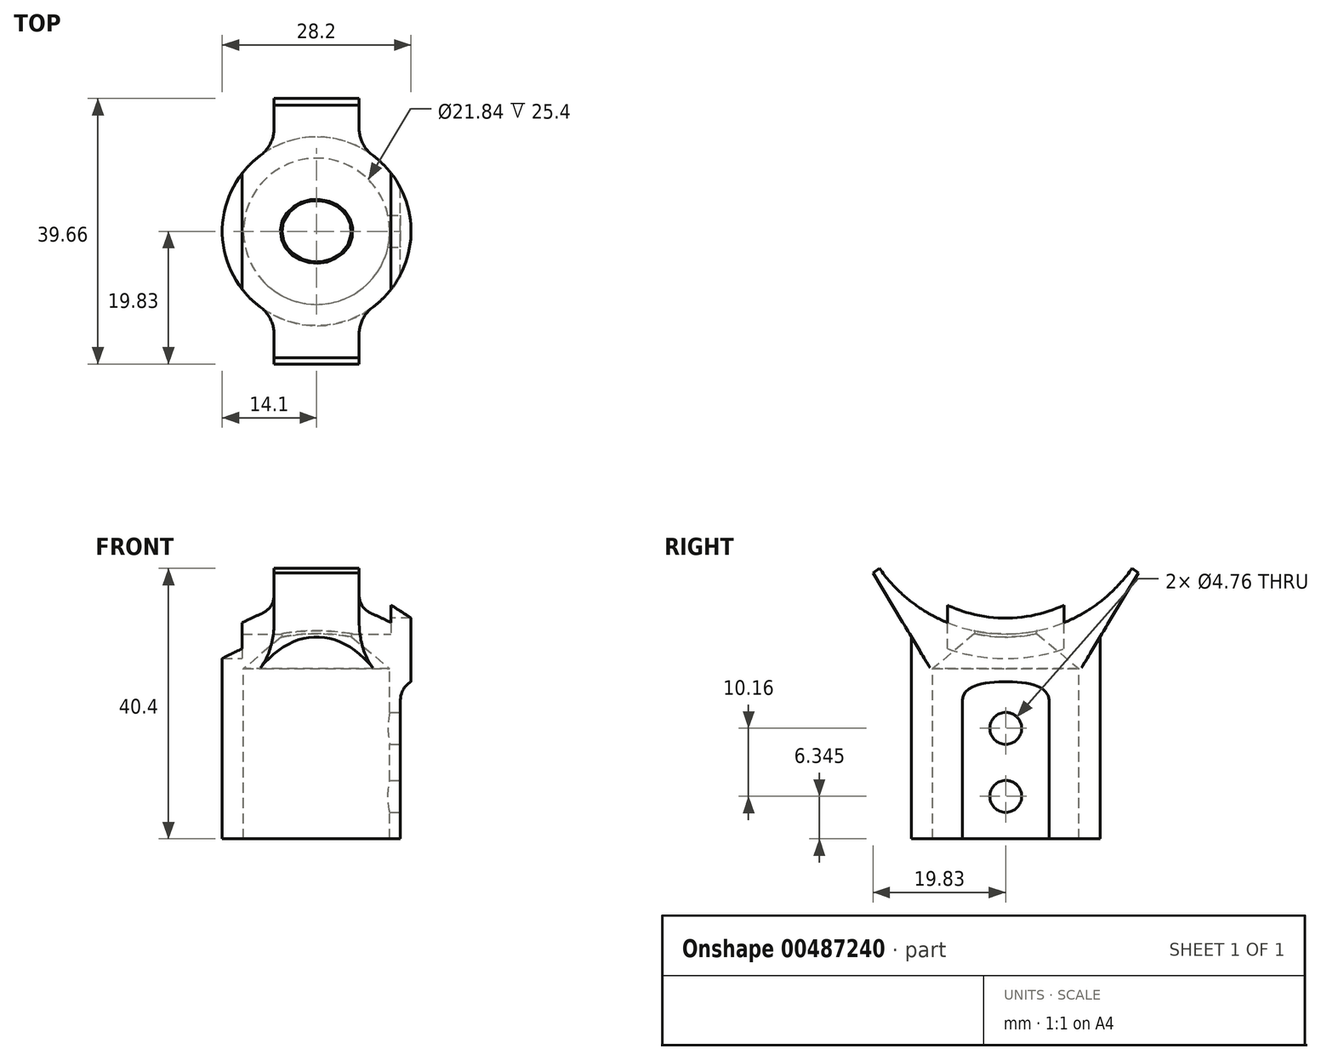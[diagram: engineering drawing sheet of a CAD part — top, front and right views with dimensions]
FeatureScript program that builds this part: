
annotation { "Feature Type Name" : "Feature", "Feature Type Description" : "" }
export const myFeature = defineFeature(function(context is Context, id is Id, definition is map)
    precondition{}
    {
        {
            var Q0;
            Q0=qCreatedBy(makeId("Front.planeOp"),FACE);
            var sketch = newSketch(context, id + "F0", { "sketchPlane" : qUnion([Q0])});
            skLineSegment(sketch, "E0", {"start": v(0, 0) * mm, "end": v(-10.92, -9.16) * mm});
            skLineSegment(sketch, "E1", {"start": v(-10.92, -9.16) * mm, "end": v(-10.92, -34.56) * mm});
            skLineSegment(sketch, "E2", {"start": v(0, 0) * mm, "end": v(0, -71.28) * mm, "construction": true});
            skLineSegment(sketch, "E3", {"start": v(-10.92, -34.56) * mm, "end": v(-14.1, -34.56) * mm});
            skLineSegment(sketch, "E4", {"start": v(-14.1, -34.56) * mm, "end": v(-14.1, 9.52) * mm});
            skLineSegment(sketch, "E5", {"start": v(-14.1, 9.52) * mm, "end": v(0, 9.52) * mm});
            skLineSegment(sketch, "E6", {"start": v(0, 9.52) * mm, "end": v(0, 0) * mm});
            skSolve(sketch);
        }
        {
            var Q0;
            Q0=makeQuery(id+"F0.imprint","IMPRINT",FACE,{"disambiguationData":[TD([[makeQuery(id+"F0.imprint","IMPRINT",EDGE,{"derivedFrom":sQuery(id+"F0.wireOp",EDGE,"E0")}),-1.0]])]});
            var Q1;
            Q1=sQuery(id+"F0.wireOp",EDGE,"E2");
            revolve(context, id + "F1", {"entities" : qUnion([Q0]), "axis" : qUnion([Q1]), "revolveType" : RevolveType.FULL});
        }
        {
            var Q0;
            Q0=makeQuery(id+"F1.opRevolve","SWEPT_EDGE",EDGE,{"disambiguationData":[OSD([sQuery(id+"F0.wireOp",EDGE,"E4"),sQuery(id+"F0.wireOp",EDGE,"E5")])]});
            fillet(context, id + "F2", {"entities" : qUnion([Q0]), "radius" : 2.38 * mm, "tangentPropagation" : true, "allowEdgeOverflow" : false});
        }
        {
            var Q0;
            Q0=qCreatedBy(makeId("Front.planeOp"),FACE);
            var sketch = newSketch(context, id + "F3", { "sketchPlane" : qUnion([Q0])});
            skLineSegment(sketch, "E7", {"start": v(10.92, -10.67) * mm, "end": v(10.92, -36.07) * mm});
            skLineSegment(sketch, "E8", {"start": v(-10.92, -36.07) * mm, "end": v(-10.92, -10.67) * mm});
            skLineSegment(sketch, "E9", {"start": v(-14.1, -36.07) * mm, "end": v(-14.1, 3.17) * mm});
            skLineSegment(sketch, "E10", {"start": v(12.5, -13.84) * mm, "end": v(12.5, -38.6) * mm});
            skLineSegment(sketch, "E11", {"start": v(15.68, -10.67) * mm, "end": v(18.86, -10.67) * mm});
            skLineSegment(sketch, "E12", {"start": v(18.86, -10.67) * mm, "end": v(18.86, -38.6) * mm});
            skLineSegment(sketch, "E13", {"start": v(18.86, -38.6) * mm, "end": v(12.5, -38.6) * mm});
            skPoint(sketch, "E14.visualSharp", {"position": v(12.5, -10.67) * mm});
            skArc(sketch, "E14.filletArc", {"start": v(15.68, -10.67) * mm, "mid": v(13.44, -11.6) * mm, "end": v(12.5, -13.84) * mm});
            skSolve(sketch);
        }
        {
            var Q0;
            Q0=makeQuery(id+"F3.imprint","IMPRINT",FACE,{"disambiguationData":[TD([[makeQuery(id+"F3.imprint","IMPRINT",EDGE,{"derivedFrom":sQuery(id+"F3.wireOp",EDGE,"E10")}),1.0]])]});
            extrude(context, id + "F4", {"entities" : qUnion([Q0]), "operationType" : NewBodyOperationType.REMOVE, "depth" : 25.4 * mm, "hasSecondDirection" : true, "secondDirectionOppositeDirection" : true, "secondDirectionDepth" : 25.4 * mm});
        }
        {
            var Q0;
            Q0=makeQuery(id+"F4.boolean.opBoolean","COPY",FACE,{"derivedFrom":makeQuery(id+"F4.opExtrude","SWEPT_FACE",FACE,{"disambiguationData":[OSD([sQuery(id+"F3.wireOp",EDGE,"E10")])]})});
            var sketch = newSketch(context, id + "F5", { "sketchPlane" : qUnion([Q0])});
            skLineSegment(sketch, "E15", {"start": v(0, -34.56) * mm, "end": v(0, -13.84) * mm, "construction": true});
            skCircle(sketch, "E16", {"center": v(0, -18.05) * mm, "radius": 2.38 * mm});
            skCircle(sketch, "E17", {"center": v(0, -28.21) * mm, "radius": 2.38 * mm});
            skSolve(sketch);
        }
        {
            var Q0;
            Q0=makeQuery(id+"F5.imprint","IMPRINT",FACE,{"disambiguationData":[TD([[makeQuery(id+"F5.imprint","IMPRINT",EDGE,{"derivedFrom":sQuery(id+"F5.wireOp",EDGE,"E16")}),1.0]])]});
            var Q1;
            Q1=makeQuery(id+"F5.imprint","IMPRINT",FACE,{"disambiguationData":[TD([[makeQuery(id+"F5.imprint","IMPRINT",EDGE,{"derivedFrom":sQuery(id+"F5.wireOp",EDGE,"E17")}),1.0]])]});
            extrude(context, id + "F6", {"entities" : qUnion([Q0, Q1]), "operationType" : NewBodyOperationType.REMOVE, "oppositeDirection" : true, "depth" : 6.35 * mm});
        }
        {
            var Q0;
            Q0=qCreatedBy(makeId("Right.planeOp"),FACE);
            var sketch = newSketch(context, id + "F7", { "sketchPlane" : qUnion([Q0])});
            skLineSegment(sketch, "E18", {"start": v(-11.12, -9.33) * mm, "end": v(0, 0) * mm});
            skLineSegment(sketch, "E19", {"start": v(0, 0) * mm, "end": v(11.12, -9.33) * mm});
            skLineSegment(sketch, "E20", {"start": v(-11.12, -9.33) * mm, "end": v(-21.59, 8.08) * mm});
            skLineSegment(sketch, "E21", {"start": v(0, 0) * mm, "end": v(0, 19.05) * mm, "construction": true});
            skLineSegment(sketch, "E22.MirrorCS", {"start": v(11.12, -9.33) * mm, "end": v(21.59, 8.08) * mm});
            skLineSegment(sketch, "E23", {"start": v(-21.6, 8.08) * mm, "end": v(21.59, 8.08) * mm});
            skCircle(sketch, "E24", {"center": v(0, 19.05) * mm, "radius": 23.03 * mm, "construction": true});
            skLineSegment(sketch, "E25", {"start": v(-15.66, 8.08) * mm, "end": v(-19.83, 5.16) * mm});
            skLineSegment(sketch, "E26.MirrorCS", {"start": v(15.66, 8.08) * mm, "end": v(19.83, 5.16) * mm});
            skPoint(sketch, "E27.orphan", {"position": v(-25.04, 1.52) * mm});
            skPoint(sketch, "E28.orphan", {"position": v(25.04, 1.52) * mm});
            skSolve(sketch);
        }
        {
            var Q0;
            Q0=makeQuery(id+"F7.imprint","IMPRINT",FACE,{"disambiguationData":[TD([[makeQuery(id+"F7.imprint","IMPRINT",EDGE,{"derivedFrom":sQuery(id+"F7.wireOp",EDGE,"E18")}),1.0]])]});
            extrude(context, id + "F8", {"entities" : qUnion([Q0]), "operationType" : NewBodyOperationType.ADD, "depth" : 6.35 * mm, "offsetDistance" : 25.4 * mm, "hasSecondDirection" : true, "secondDirectionOppositeDirection" : true, "secondDirectionDepth" : 6.35 * mm});
        }
        {
            var Q0;
            Q0=qCreatedBy(makeId("Right.planeOp"),FACE);
            var sketch = newSketch(context, id + "F9", { "sketchPlane" : qUnion([Q0])});
            skCircle(sketch, "E29.0", {"center": v(0, 19.05) * mm, "radius": 23.03 * mm});
            skSolve(sketch);
        }
        {
            var Q0;
            Q0=makeQuery(id+"F9.imprint","IMPRINT",FACE,{"disambiguationData":[TD([[makeQuery(id+"F9.imprint","IMPRINT",EDGE,{"derivedFrom":sQuery(id+"F9.wireOp",EDGE,"E29.0")}),1.0]])]});
            extrude(context, id + "F10", {"entities" : qUnion([Q0]), "operationType" : NewBodyOperationType.REMOVE, "oppositeDirection" : true, "depth" : 25.4 * mm, "offsetDistance" : 25.4 * mm, "hasSecondDirection" : true, "secondDirectionOppositeDirection" : false, "secondDirectionDepth" : 11.1 * mm});
        }
        {
            var Q0;
            Q0=makeQuery(id+"F8.boolean.opBoolean","INTERSECT",EDGE,{"disambiguationData":[OD(0.0)],"derivedFrom":[makeQuery(id+"F1.opRevolve","SWEPT_FACE",FACE,{"disambiguationData":[OSD([sQuery(id+"F0.wireOp",EDGE,"E4")])]}),makeQuery(id+"F8.opExtrude","CAP_FACE",FACE,{"disambiguationData":[OSD([sQuery(id+"F7.wireOp",EDGE,"E18"),sQuery(id+"F7.wireOp",EDGE,"E19"),sQuery(id+"F7.wireOp",EDGE,"E20"),sQuery(id+"F7.wireOp",EDGE,"E22.MirrorCS"),sQuery(id+"F7.wireOp",EDGE,"E23")])],"isStart":false})]});
            var Q1;
            Q1=makeQuery(id+"F8.boolean.opBoolean","INTERSECT",EDGE,{"disambiguationData":[OD(1.0)],"derivedFrom":[makeQuery(id+"F1.opRevolve","SWEPT_FACE",FACE,{"disambiguationData":[OSD([sQuery(id+"F0.wireOp",EDGE,"E4")])]}),makeQuery(id+"F8.opExtrude","CAP_FACE",FACE,{"disambiguationData":[OSD([sQuery(id+"F7.wireOp",EDGE,"E18"),sQuery(id+"F7.wireOp",EDGE,"E19"),sQuery(id+"F7.wireOp",EDGE,"E20"),sQuery(id+"F7.wireOp",EDGE,"E22.MirrorCS"),sQuery(id+"F7.wireOp",EDGE,"E23")])],"isStart":false})]});
            var Q2;
            Q2=makeQuery(id+"F8.boolean.opBoolean","INTERSECT",EDGE,{"disambiguationData":[OD(1.0)],"derivedFrom":[makeQuery(id+"F1.opRevolve","SWEPT_FACE",FACE,{"disambiguationData":[OSD([sQuery(id+"F0.wireOp",EDGE,"E4")])]}),makeQuery(id+"F8.opExtrude","CAP_FACE",FACE,{"disambiguationData":[OSD([sQuery(id+"F7.wireOp",EDGE,"E18"),sQuery(id+"F7.wireOp",EDGE,"E19"),sQuery(id+"F7.wireOp",EDGE,"E20"),sQuery(id+"F7.wireOp",EDGE,"E22.MirrorCS"),sQuery(id+"F7.wireOp",EDGE,"E23")])],"isStart":true})]});
            var Q3;
            Q3=makeQuery(id+"F8.boolean.opBoolean","INTERSECT",EDGE,{"disambiguationData":[OD(0.0)],"derivedFrom":[makeQuery(id+"F1.opRevolve","SWEPT_FACE",FACE,{"disambiguationData":[OSD([sQuery(id+"F0.wireOp",EDGE,"E4")])]}),makeQuery(id+"F8.opExtrude","CAP_FACE",FACE,{"disambiguationData":[OSD([sQuery(id+"F7.wireOp",EDGE,"E18"),sQuery(id+"F7.wireOp",EDGE,"E19"),sQuery(id+"F7.wireOp",EDGE,"E20"),sQuery(id+"F7.wireOp",EDGE,"E22.MirrorCS"),sQuery(id+"F7.wireOp",EDGE,"E23")])],"isStart":true})]});
            fillet(context, id + "F11", {"entities" : qUnion([Q0, Q1, Q2, Q3]), "radius" : 5.08 * mm, "tangentPropagation" : true, "allowEdgeOverflow" : false});
        }
        {
            var Q0;
            Q0=qCreatedBy(makeId("Right.planeOp"),FACE);
            var sketch = newSketch(context, id + "F12", { "sketchPlane" : qUnion([Q0])});
            skCircle(sketch, "E30", {"center": v(0, 19.05) * mm, "radius": 20.64 * mm});
            skSolve(sketch);
        }
        {
            var Q0;
            Q0=makeQuery(id+"F12.imprint","IMPRINT",FACE,{"disambiguationData":[TD([[makeQuery(id+"F12.imprint","IMPRINT",EDGE,{"derivedFrom":sQuery(id+"F12.wireOp",EDGE,"E30")}),1.0]])]});
            extrude(context, id + "F13", {"entities" : qUnion([Q0]), "operationType" : NewBodyOperationType.REMOVE, "depth" : 25.4 * mm, "offsetDistance" : 25.4 * mm});
        }
        {
            var Q0;
            Q0=qCreatedBy(makeId("Right.planeOp"),FACE);
            cPlane(context, id + "F14", {"entities" : qUnion([Q0]), "cplaneType" : CPlaneType.OFFSET, "offset" : 11.1 * mm, "oppositeDirection" : true, "width" : 152.4 * mm, "height" : 152.4 * mm});
        }
        {
            var Q0;
            Q0=qCreatedBy(id+"F14.planeOp",FACE);
            var sketch = newSketch(context, id + "F15", { "sketchPlane" : qUnion([Q0])});
            skPoint(sketch, "E31.0", {"position": v(0, 19.05) * mm});
            skCircle(sketch, "E32", {"center": v(0, 19.05) * mm, "radius": 26.67 * mm});
            skSolve(sketch);
        }
        {
            var Q0;
            Q0=makeQuery(id+"F15.imprint","IMPRINT",FACE,{"disambiguationData":[TD([[makeQuery(id+"F15.imprint","IMPRINT",EDGE,{"derivedFrom":sQuery(id+"F15.wireOp",EDGE,"E32")}),1.0]])]});
            extrude(context, id + "F16", {"entities" : qUnion([Q0]), "operationType" : NewBodyOperationType.REMOVE, "oppositeDirection" : true, "depth" : 25.4 * mm, "offsetDistance" : 25.4 * mm});
        }
        {
            var Q0;
            Q0=makeQuery(id+"F10.boolean.opBoolean","INTERSECT",EDGE,{"derivedFrom":[makeQuery(id+"F1.opRevolve","SWEPT_FACE",FACE,{"disambiguationData":[OSD([sQuery(id+"F0.wireOp",EDGE,"E0")])]}),makeQuery(id+"F10.opExtrude","SWEPT_FACE",FACE,{"disambiguationData":[OSD([sQuery(id+"F9.wireOp",EDGE,"E29.0")])]})]});
            fillet(context, id + "F17", {"entities" : qUnion([Q0]), "radius" : 0.25 * mm, "tangentPropagation" : true, "allowEdgeOverflow" : false});
        }
    });
